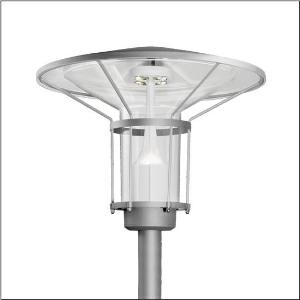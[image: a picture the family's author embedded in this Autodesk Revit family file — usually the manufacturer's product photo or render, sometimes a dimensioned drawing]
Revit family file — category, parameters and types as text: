
# Revit family: laterne_classic_iq___p1_0a_5xa5245lf14hp_1a7c
name_source: partatom
category: Lighting Fixtures
units: mm (PartAtom-declared; Revit-internal decimal feet)

## family parameters
Cut with Voids When Loaded = No
Host = Face
Light Source = No
Part Type = Normal
Room Calculation Point = No
Round Connector Dimension = Use Diameter
Shared = No

## types (1)
- --- (1 x LED, 4400 lm, 33.6 W, 4000K)
    Apparent Load = 34 VA
    CIE Flux Codes = 31 61 91 96 100
    Color Rendering = 70
    Color Temperature = 4000K
    Default Elevation = 1800 mm
    Description = Lantern Classic iQ, mast luminaire, Module 540 iQ-SR, primary light control with 3 zone facetted reflector, of plastic, silver coated, highly specular, structured, primary optical cover: cover, of PMMA, transparent, light distribution: P1.0a, light emission: direct distribution, primary light characteristic: strongly asymmetric, installation type: post-top, LED, High Power LED, rated luminous flux: 4.400lm, luminous efficacy: 131lm/W, light colour: 740, colour temperature: 4000K, control gear: ECG iQ, control: pre-setting: logarithmic dimming characteristic, Street-Remote, Auto-Match, Temp-Guard, Lumen-Switch, Night-Set, Smart-Wire, Light-Fading, Desk-Remote (wireless, voltage-free reading and setting of iQ features in the workshop via application-optimized NFC function/RFID function), optimised constant luminous flux control (CLO 2.0), with terminal, 6-pole, max. 2.5mm², mains connection: 230..240V, AC, 50/60Hz, start of lifetime: 34W, end of service life: 36W, reduction: 15W, luminaire housing, upper part, of glass-fibre reinforced polyester, coated, Siteco® metallic grey (DB 702S), diameter: 750mm, height: 596mm, spigot size: d x l = 76 x 70mm (post-top) | with reducer (optional accessory) 60 x 70mm, post-top mast mounting element, of diecast aluminium, coated, Siteco® metallic grey (DB 702S), Module 540 iQ-SR, traffic white (RAL 9016), equipment: Power, protection rating (complete): IP65, insulation class (complete): insulation class II (safety insulation), certification: CE, ENEC, VDE, packaging unit: 1 piece

Light Distribution: P1.0a
    Height = 596 mm
    Lamp = 1 x LED
    Lamp Light Flux = 4400 lm
    Lamp Power = 33.6 W
    Lamp count = 1
    Length = 750 mm
    Luminous efficacy = 131 lm/W
    Manufacturer = Siteco
    ModVariant = No
    Model = 5XA5245LF14HP
    Number of Poles = 1
    OnlyDefault = Yes
    Power Factor = 1
    Product Name = Laterne Classic iQ | P1.0a
    Product group = mast luminaire | pylon top
    ProductGroupID = 6100
    Protection Class = Protection class II
    Protection Degree = IP 65
    RLX_Detail_Level = 1
    RLX_Emergency_Light_Flux = 0 lm
    RLX_Emergency_Type = 0
    RLX_Emergency_Type_DB = No
    RlxData = <blob elided: 65561 chars, md5=739a0261>
    Socket = socket
    Standby Power = 0 W
    System Light Flux = 4400 lm
    System Power = 34 W
    Type Comments = factory setting: luminous flux: 100 % | dim-lin: 254 | 695 mA
    Type Image = l_1006052.jpg
    URL = http://relux.com
    VarID = @adj_165811
    Voltage = 0 V
    Weight = 0.00 kg
    Width = 0 mm  [stored 0 ft]

note: [stored X ft] marks values corroborated as IEEE doubles in the binary element streams (Revit-internal decimal feet)

## geometry (parser evidence)
native form markers: Blend x4, Sweep x9
no freeform markers — native parametric forms only
